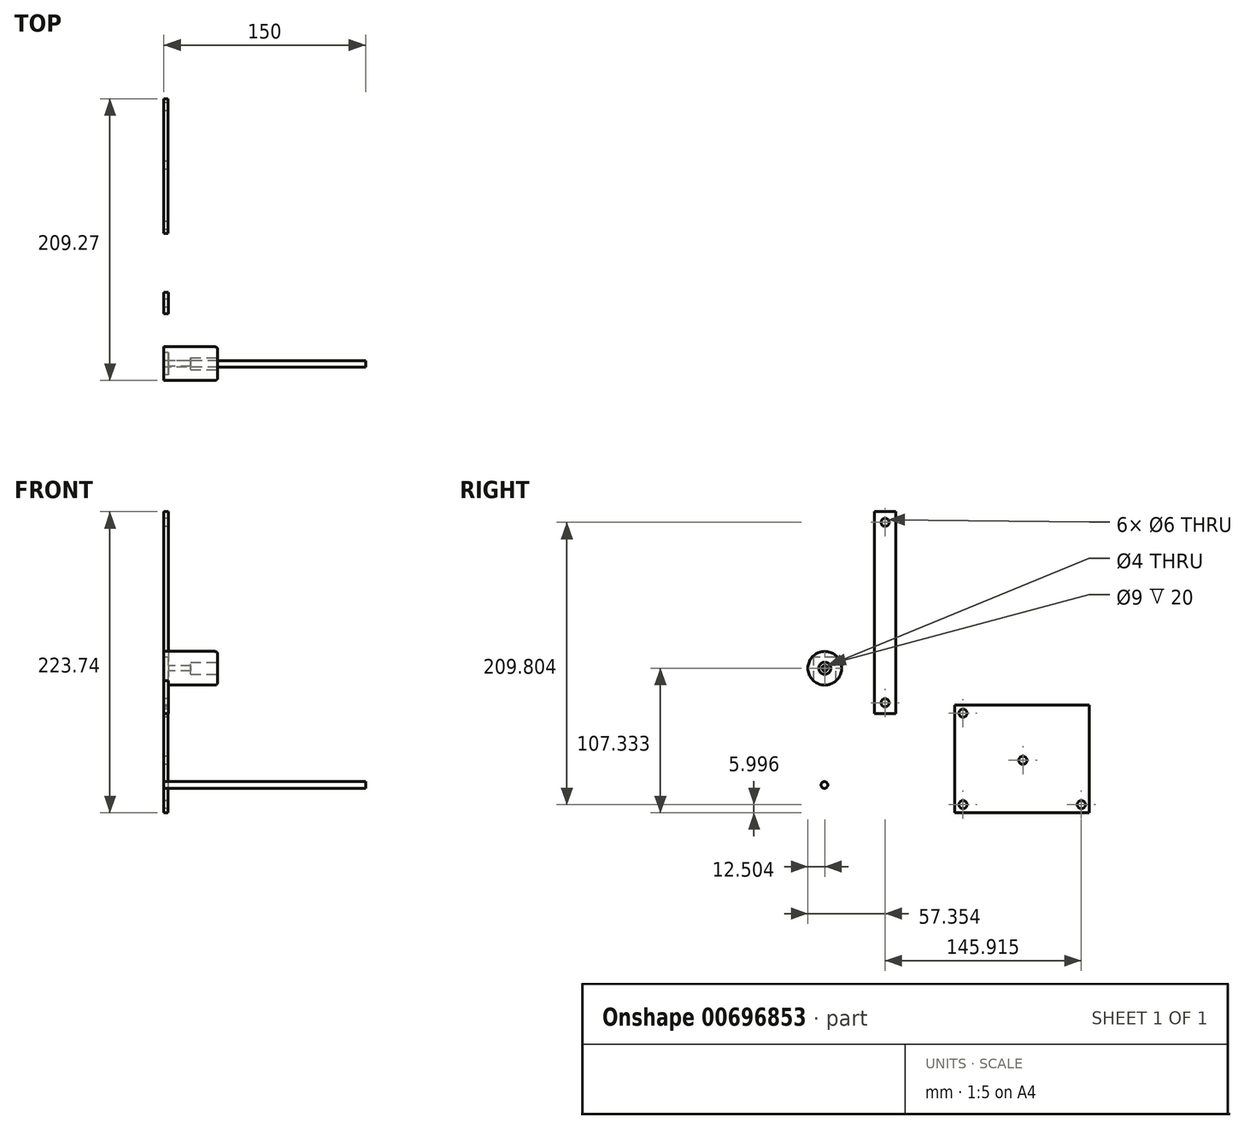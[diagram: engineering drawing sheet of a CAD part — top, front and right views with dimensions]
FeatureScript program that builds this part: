
annotation { "Feature Type Name" : "Feature", "Feature Type Description" : "" }
export const myFeature = defineFeature(function(context is Context, id is Id, definition is map)
    precondition{}
    {
        {
            assignVariable(context, id + "F0", {"name" : "flatbarthickness", "anyValue" : 3.25});
        }
        {
            assignVariable(context, id + "F1", {"name" : "perspexthickness", "anyValue" : 3});
        }
        {
            var Q0;
            Q0=qCreatedBy(makeId("Right.planeOp"),FACE);
            var sketch = newSketch(context, id + "F2", { "sketchPlane" : qUnion([Q0])});
            skLineSegment(sketch, "E0.bottom", {"start": v(-15.3, 150) * mm, "end": v(0.57, 150) * mm});
            skLineSegment(sketch, "E0.top", {"start": v(-15.3, 0) * mm, "end": v(0.57, 0) * mm});
            skLineSegment(sketch, "E0.left", {"start": v(-15.3, 150) * mm, "end": v(-15.3, 0) * mm});
            skLineSegment(sketch, "E0.right", {"start": v(0.57, 150) * mm, "end": v(0.57, 0) * mm});
            skCircle(sketch, "E1", {"center": v(-7.37, 7.94) * mm, "radius": 3 * mm});
            skCircle(sketch, "E2", {"center": v(-7.37, 142.06) * mm, "radius": 3 * mm});
            skSolve(sketch);
        }
        {
            var Q0;
            Q0=makeQuery(id+"F2.imprint","IMPRINT",FACE,{"disambiguationData":[TD([[makeQuery(id+"F2.imprint","IMPRINT",EDGE,{"derivedFrom":sQuery(id+"F2.wireOp",EDGE,"E0.bottom")}),-1.0]])]});
            extrude(context, id + "F3", {"entities" : qUnion([Q0]), "depth" : (getVariable(context, 'flatbarthickness')) * mm, "offsetDistance" : 25 * mm});
        }
        {
            var Q0;
            Q0=qCreatedBy(makeId("Right.planeOp"),FACE);
            var sketch = newSketch(context, id + "F4", { "sketchPlane" : qUnion([Q0])});
            skCircle(sketch, "E3", {"center": v(-52.22, 33.6) * mm, "radius": 12.5 * mm});
            skSolve(sketch);
        }
        {
            var Q0;
            Q0=makeQuery(id+"F4.imprint","IMPRINT",FACE,{"disambiguationData":[TD([[makeQuery(id+"F4.imprint","IMPRINT",EDGE,{"derivedFrom":sQuery(id+"F4.wireOp",EDGE,"E3")}),1.0]])]});
            extrude(context, id + "F5", {"entities" : qUnion([Q0]), "depth" : 40 * mm, "offsetDistance" : 25 * mm});
        }
        {
            var Q0;
            Q0=makeQuery(id+"F5.opExtrude","CAP_FACE",FACE,{"disambiguationData":[OSD([sQuery(id+"F4.wireOp",EDGE,"E3")])],"isStart":true});
            var sketch = newSketch(context, id + "F6", { "sketchPlane" : qUnion([Q0])});
            skCircle(sketch, "E4", {"center": v(52.22, 33.6) * mm, "radius": 2 * mm});
            skSolve(sketch);
        }
        {
            var Q0;
            Q0 = qSketchRegion(id + "F6", true);
            extrude(context, id + "F7", {"entities" : qUnion([Q0]), "operationType" : NewBodyOperationType.REMOVE, "endBound" : BoundingType.UP_TO_NEXT, "oppositeDirection" : true, "depth" : 25 * mm, "offsetDistance" : 25 * mm});
        }
        {
            var Q0;
            Q0=makeQuery(id+"F5.opExtrude","CAP_FACE",FACE,{"disambiguationData":[OSD([sQuery(id+"F4.wireOp",EDGE,"E3")])],"isStart":false});
            var sketch = newSketch(context, id + "F8", { "sketchPlane" : qUnion([Q0])});
            skCircle(sketch, "E5", {"center": v(-52.22, 33.6) * mm, "radius": 4.5 * mm});
            skSolve(sketch);
        }
        {
            var Q0;
            Q0=makeQuery(id+"F8.imprint","IMPRINT",FACE,{"disambiguationData":[TD([[makeQuery(id+"F8.imprint","IMPRINT",EDGE,{"derivedFrom":sQuery(id+"F8.wireOp",EDGE,"E5")}),1.0]])]});
            var Q1;
            Q1=sQuery(id+"F8.wireOp",EDGE,"E5");
            extrude(context, id + "F9", {"entities" : qUnion([Q0]), "operationType" : NewBodyOperationType.REMOVE, "surfaceEntities" : qUnion([Q1]), "oppositeDirection" : true, "depth" : 20 * mm, "offsetDistance" : 25 * mm});
        }
        {
            var Q0;
            Q0=makeQuery(id+"F5.opExtrude","CAP_EDGE",EDGE,{"disambiguationData":[OSD([sQuery(id+"F4.wireOp",EDGE,"E3")])],"isStart":false});
            fillet(context, id + "F10", {"entities" : qUnion([Q0]), "radius" : 2 * mm, "tangentPropagation" : true, "allowEdgeOverflow" : false});
        }
        {
            var Q0;
            Q0=makeQuery(id+"F5.opExtrude","CAP_FACE",FACE,{"disambiguationData":[OSD([sQuery(id+"F4.wireOp",EDGE,"E3")])],"isStart":true});
            var sketch = newSketch(context, id + "F11", { "sketchPlane" : qUnion([Q0])});
            skLineSegment(sketch, "E6.bottom", {"start": v(43.97, 16.84) * mm, "end": v(60.47, 16.84) * mm});
            skLineSegment(sketch, "E6.top", {"start": v(43.97, 41.84) * mm, "end": v(60.47, 41.84) * mm});
            skLineSegment(sketch, "E6.left", {"start": v(43.97, 16.84) * mm, "end": v(43.97, 41.84) * mm});
            skLineSegment(sketch, "E6.right", {"start": v(60.47, 16.84) * mm, "end": v(60.47, 41.84) * mm});
            skSolve(sketch);
        }
        {
            var Q0;
            {var subQ1=sQuery(id+"F11.wireOp",EDGE,"E6.top");Q0=makeQuery(id+"F11.imprint","IMPRINT",FACE,{"disambiguationData":[TD([[makeQuery(id+"F11.imprint","IMPRINT",EDGE,{"derivedFrom":subQ1}),-1.0]])]});}
            extrude(context, id + "F12", {"entities" : qUnion([Q0]), "operationType" : NewBodyOperationType.REMOVE, "oppositeDirection" : true, "depth" : 3.25 * mm, "offsetDistance" : 25 * mm});
        }
        {
            var Q0;
            Q0=qCreatedBy(makeId("Right.planeOp"),FACE);
            var sketch = newSketch(context, id + "F13", { "sketchPlane" : qUnion([Q0])});
            skCircle(sketch, "E7", {"center": v(-52.46, -53.15) * mm, "radius": 2.5 * mm});
            skSolve(sketch);
        }
        {
            var Q0;
            Q0=makeQuery(id+"F13.imprint","IMPRINT",FACE,{"disambiguationData":[TD([[makeQuery(id+"F13.imprint","IMPRINT",EDGE,{"derivedFrom":sQuery(id+"F13.wireOp",EDGE,"E7")}),1.0]])]});
            extrude(context, id + "F14", {"entities" : qUnion([Q0]), "depth" : 150 * mm, "offsetDistance" : 25 * mm});
        }
        {
            var Q0;
            Q0=qCreatedBy(makeId("Right.planeOp"),FACE);
            var sketch = newSketch(context, id + "F15", { "sketchPlane" : qUnion([Q0])});
            skLineSegment(sketch, "E8.bottom", {"start": v(144.55, 6.26) * mm, "end": v(44.55, 6.26) * mm});
            skLineSegment(sketch, "E8.top", {"start": v(144.55, -73.74) * mm, "end": v(44.55, -73.74) * mm});
            skLineSegment(sketch, "E8.left", {"start": v(144.55, 6.26) * mm, "end": v(144.55, -73.74) * mm});
            skLineSegment(sketch, "E8.right", {"start": v(44.55, 6.26) * mm, "end": v(44.55, -73.74) * mm});
            skCircle(sketch, "E9", {"center": v(50.55, 0.26) * mm, "radius": 3 * mm});
            skCircle(sketch, "E10", {"center": v(138.55, -67.74) * mm, "radius": 3 * mm});
            skCircle(sketch, "E11", {"center": v(50.55, -67.74) * mm, "radius": 3 * mm});
            skCircle(sketch, "E12", {"center": v(95.05, -34.81) * mm, "radius": 3 * mm});
            skSolve(sketch);
        }
        {
            var Q0;
            Q0=makeQuery(id+"F15.imprint","IMPRINT",FACE,{"disambiguationData":[TD([[makeQuery(id+"F15.imprint","IMPRINT",EDGE,{"derivedFrom":sQuery(id+"F15.wireOp",EDGE,"E8.bottom")}),1.0]])]});
            extrude(context, id + "F16", {"entities" : qUnion([Q0]), "depth" : (getVariable(context, 'perspexthickness')) * mm, "offsetDistance" : 25 * mm});
        }
    });
